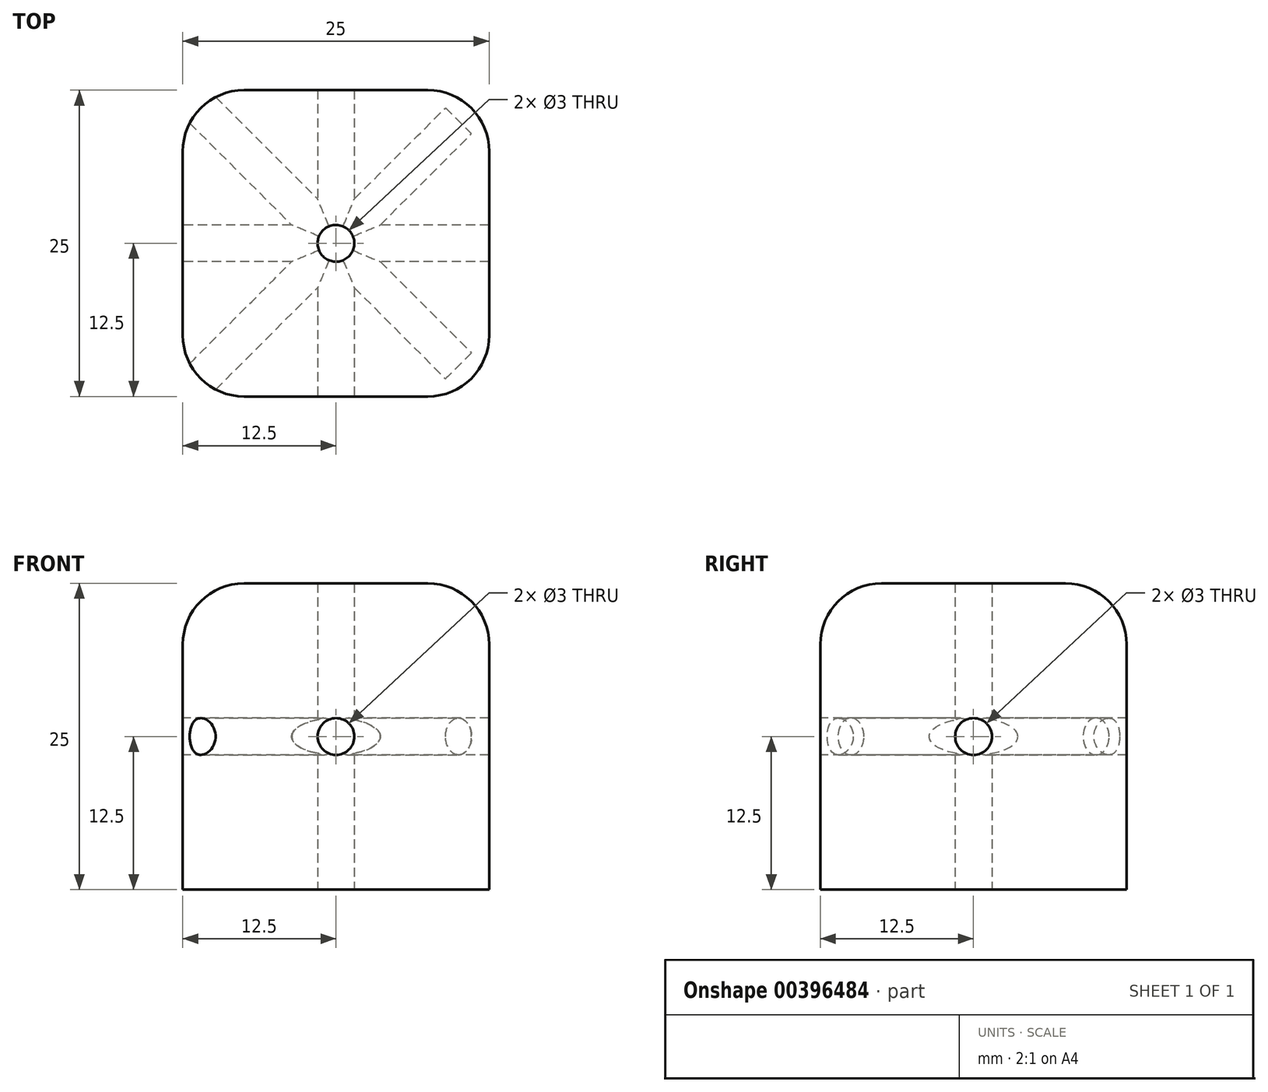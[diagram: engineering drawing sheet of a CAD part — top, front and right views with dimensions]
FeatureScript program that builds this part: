
annotation { "Feature Type Name" : "Feature", "Feature Type Description" : "" }
export const myFeature = defineFeature(function(context is Context, id is Id, definition is map)
    precondition{}
    {
        {
            var Q0;
            Q0=qCreatedBy(makeId("Front.planeOp"),FACE);
            var sketch = newSketch(context, id + "F0", { "sketchPlane" : qUnion([Q0])});
            skLineSegment(sketch, "E0.bottom", {"start": v(-12.5, -12.5) * mm, "end": v(12.5, -12.5) * mm});
            skLineSegment(sketch, "E0.top", {"start": v(-12.5, 12.5) * mm, "end": v(12.5, 12.5) * mm});
            skLineSegment(sketch, "E0.left", {"start": v(-12.5, -12.5) * mm, "end": v(-12.5, 12.5) * mm});
            skLineSegment(sketch, "E0.right", {"start": v(12.5, -12.5) * mm, "end": v(12.5, 12.5) * mm});
            skPoint(sketch, "E0.middle", {"position": v(0, 0) * mm});
            skSolve(sketch);
        }
        {
            var Q0;
            Q0=makeQuery(id+"F0.imprint","IMPRINT",FACE,{"disambiguationData":[TD([[makeQuery(id+"F0.imprint","IMPRINT",EDGE,{"derivedFrom":sQuery(id+"F0.wireOp",EDGE,"E0.bottom")}),1.0]])]});
            extrude(context, id + "F1", {"entities" : qUnion([Q0]), "endBound" : BoundingType.SYMMETRIC, "depth" : 25 * mm});
        }
        {
            var Q0;
            Q0=makeQuery(id+"F1.opExtrude","CAP_FACE",FACE,{"disambiguationData":[OSD([sQuery(id+"F0.wireOp",EDGE,"E0.bottom"),sQuery(id+"F0.wireOp",EDGE,"E0.top"),sQuery(id+"F0.wireOp",EDGE,"E0.left"),sQuery(id+"F0.wireOp",EDGE,"E0.right")])],"isStart":false});
            var sketch = newSketch(context, id + "F2", { "sketchPlane" : qUnion([Q0])});
            skCircle(sketch, "E1", {"center": v(0, 0) * mm, "radius": 1.5 * mm});
            skSolve(sketch);
        }
        {
            var Q0;
            Q0 = qSketchRegion(id + "F2", true);
            extrude(context, id + "F3", {"entities" : qUnion([Q0]), "operationType" : NewBodyOperationType.REMOVE, "endBound" : BoundingType.UP_TO_NEXT, "oppositeDirection" : true, "depth" : 25 * mm});
        }
        {
            var Q0;
            Q0=makeQuery(id+"F1.opExtrude","SWEPT_FACE",FACE,{"disambiguationData":[OSD([sQuery(id+"F0.wireOp",EDGE,"E0.bottom")])]});
            var sketch = newSketch(context, id + "F4", { "sketchPlane" : qUnion([Q0])});
            skCircle(sketch, "E2", {"center": v(0, 0) * mm, "radius": 1.5 * mm});
            skSolve(sketch);
        }
        {
            var Q0;
            Q0 = qSketchRegion(id + "F4", true);
            extrude(context, id + "F5", {"entities" : qUnion([Q0]), "operationType" : NewBodyOperationType.REMOVE, "endBound" : BoundingType.THROUGH_ALL, "oppositeDirection" : true, "depth" : 25 * mm});
        }
        {
            var Q0;
            Q0=makeQuery(id+"F1.opExtrude","SWEPT_FACE",FACE,{"disambiguationData":[OSD([sQuery(id+"F0.wireOp",EDGE,"E0.left")])]});
            var sketch = newSketch(context, id + "F6", { "sketchPlane" : qUnion([Q0])});
            skCircle(sketch, "E3", {"center": v(0, 0) * mm, "radius": 1.5 * mm});
            skSolve(sketch);
        }
        {
            var Q0;
            Q0=makeQuery(id+"F6.imprint","IMPRINT",FACE,{"disambiguationData":[TD([[makeQuery(id+"F6.imprint","IMPRINT",EDGE,{"derivedFrom":sQuery(id+"F6.wireOp",EDGE,"E3")}),1.0]])]});
            extrude(context, id + "F7", {"entities" : qUnion([Q0]), "operationType" : NewBodyOperationType.REMOVE, "endBound" : BoundingType.THROUGH_ALL, "oppositeDirection" : true, "depth" : 25 * mm});
        }
        {
            var Q0;
            Q0=makeQuery(id+"F1.opExtrude","CAP_EDGE",EDGE,{"disambiguationData":[OSD([sQuery(id+"F0.wireOp",EDGE,"E0.right")])],"isStart":false});
            var Q1;
            Q1=makeQuery(id+"F1.opExtrude","SWEPT_EDGE",EDGE,{"disambiguationData":[OSD([sQuery(id+"F0.wireOp",EDGE,"E0.top"),sQuery(id+"F0.wireOp",EDGE,"E0.right")])]});
            var Q2;
            Q2=makeQuery(id+"F1.opExtrude","CAP_EDGE",EDGE,{"disambiguationData":[OSD([sQuery(id+"F0.wireOp",EDGE,"E0.top")])],"isStart":true});
            var Q3;
            Q3=makeQuery(id+"F1.opExtrude","CAP_EDGE",EDGE,{"disambiguationData":[OSD([sQuery(id+"F0.wireOp",EDGE,"E0.left")])],"isStart":true});
            var Q4;
            Q4=makeQuery(id+"F1.opExtrude","SWEPT_EDGE",EDGE,{"disambiguationData":[OSD([sQuery(id+"F0.wireOp",EDGE,"E0.top"),sQuery(id+"F0.wireOp",EDGE,"E0.left")])]});
            var Q5;
            Q5=makeQuery(id+"F1.opExtrude","CAP_EDGE",EDGE,{"disambiguationData":[OSD([sQuery(id+"F0.wireOp",EDGE,"E0.left")])],"isStart":false});
            var Q6;
            Q6=makeQuery(id+"F1.opExtrude","CAP_EDGE",EDGE,{"disambiguationData":[OSD([sQuery(id+"F0.wireOp",EDGE,"E0.top")])],"isStart":false});
            var Q7;
            Q7=makeQuery(id+"F1.opExtrude","CAP_EDGE",EDGE,{"disambiguationData":[OSD([sQuery(id+"F0.wireOp",EDGE,"E0.right")])],"isStart":true});
            fillet(context, id + "F8", {"entities" : qUnion([Q0, Q1, Q2, Q3, Q4, Q5, Q6, Q7]), "radius" : 5 * mm, "tangentPropagation" : true, "allowEdgeOverflow" : false});
        }
        {
            var Q0;
            {var subQ0=sQuery(id+"F0.wireOp",EDGE,"E0.right");var subQ1=sQuery(id+"F0.wireOp",EDGE,"E0.top");Q0=makeQuery(id+"F8.opFillet","BLEND_VERTEX",VERTEX,{"blendedFrom":[makeQuery(id+"F1.opExtrude","CAP_VERTEX",VERTEX,{"disambiguationData":[OSD([subQ1,subQ0])],"isStart":true}),makeQuery(id+"F1.opExtrude","SWEPT_EDGE",EDGE,{"disambiguationData":[OSD([subQ1,subQ0])]}),makeQuery(id+"F1.opExtrude","CAP_EDGE",EDGE,{"disambiguationData":[OSD([subQ0])],"isStart":true}),makeQuery(id+"F1.opExtrude","SWEPT_FACE",FACE,{"disambiguationData":[OSD([subQ0])]})],"blendedInto":[makeQuery(id+"F1.opExtrude","SWEPT_FACE",FACE,{"disambiguationData":[OSD([subQ0])]})]});}
            var Q1;
            {var subQ0=sQuery(id+"F0.wireOp",EDGE,"E0.right");var subQ1=sQuery(id+"F0.wireOp",EDGE,"E0.top");Q1=makeQuery(id+"F8.opFillet","BLEND_VERTEX",VERTEX,{"blendedFrom":[makeQuery(id+"F1.opExtrude","CAP_VERTEX",VERTEX,{"disambiguationData":[OSD([subQ1,subQ0])],"isStart":true}),makeQuery(id+"F1.opExtrude","CAP_EDGE",EDGE,{"disambiguationData":[OSD([subQ1])],"isStart":true}),makeQuery(id+"F1.opExtrude","CAP_EDGE",EDGE,{"disambiguationData":[OSD([subQ0])],"isStart":true}),makeQuery(id+"F1.opExtrude","CAP_FACE",FACE,{"disambiguationData":[OSD([sQuery(id+"F0.wireOp",EDGE,"E0.bottom"),subQ1,sQuery(id+"F0.wireOp",EDGE,"E0.left"),subQ0])],"isStart":true})],"blendedInto":[makeQuery(id+"F1.opExtrude","CAP_FACE",FACE,{"disambiguationData":[OSD([sQuery(id+"F0.wireOp",EDGE,"E0.bottom"),subQ1,sQuery(id+"F0.wireOp",EDGE,"E0.left"),subQ0])],"isStart":true})]});}
            var Q2;
            {var subQ0=sQuery(id+"F0.wireOp",EDGE,"E0.right");Q2=makeQuery(id+"F8.opFillet","BLEND_VERTEX",VERTEX,{"blendedFrom":[makeQuery(id+"F1.opExtrude","CAP_EDGE",EDGE,{"disambiguationData":[OSD([subQ0])],"isStart":true}),makeQuery(id+"F1.opExtrude","SWEPT_FACE",FACE,{"disambiguationData":[OSD([sQuery(id+"F0.wireOp",EDGE,"E0.bottom")])]}),makeQuery(id+"F1.opExtrude","SWEPT_FACE",FACE,{"disambiguationData":[OSD([subQ0])]})],"blendedInto":[makeQuery(id+"F1.opExtrude","SWEPT_FACE",FACE,{"disambiguationData":[OSD([sQuery(id+"F0.wireOp",EDGE,"E0.bottom")])]}),makeQuery(id+"F1.opExtrude","SWEPT_FACE",FACE,{"disambiguationData":[OSD([subQ0])]})]});}
            cPlane(context, id + "F9", {"entities" : qUnion([Q0, Q1, Q2]), "cplaneType" : CPlaneType.THREE_POINT, "offset" : 25 * mm, "width" : 150 * mm, "height" : 150 * mm});
        }
        {
            var Q0;
            Q0=qCreatedBy(id+"F9.planeOp",FACE);
            var sketch = newSketch(context, id + "F10", { "sketchPlane" : qUnion([Q0])});
            skCircle(sketch, "E4", {"center": v(0, 0) * mm, "radius": 1.5 * mm});
            skSolve(sketch);
        }
        {
            var Q0;
            Q0 = qSketchRegion(id + "F10", true);
            extrude(context, id + "F11", {"entities" : qUnion([Q0]), "operationType" : NewBodyOperationType.REMOVE, "endBound" : BoundingType.THROUGH_ALL, "oppositeDirection" : true, "depth" : 25 * mm});
        }
        {
            var Q0;
            {var subQ0=sQuery(id+"F0.wireOp",EDGE,"E0.right");var subQ1=sQuery(id+"F0.wireOp",EDGE,"E0.top");Q0=makeQuery(id+"F8.opFillet","BLEND_VERTEX",VERTEX,{"blendedFrom":[makeQuery(id+"F1.opExtrude","CAP_VERTEX",VERTEX,{"disambiguationData":[OSD([subQ1,subQ0])],"isStart":false}),makeQuery(id+"F1.opExtrude","CAP_EDGE",EDGE,{"disambiguationData":[OSD([subQ1])],"isStart":false}),makeQuery(id+"F1.opExtrude","CAP_EDGE",EDGE,{"disambiguationData":[OSD([subQ0])],"isStart":false}),makeQuery(id+"F1.opExtrude","CAP_FACE",FACE,{"disambiguationData":[OSD([sQuery(id+"F0.wireOp",EDGE,"E0.bottom"),subQ1,sQuery(id+"F0.wireOp",EDGE,"E0.left"),subQ0])],"isStart":false})],"blendedInto":[makeQuery(id+"F1.opExtrude","CAP_FACE",FACE,{"disambiguationData":[OSD([sQuery(id+"F0.wireOp",EDGE,"E0.bottom"),subQ1,sQuery(id+"F0.wireOp",EDGE,"E0.left"),subQ0])],"isStart":false})]});}
            var Q1;
            {var subQ0=sQuery(id+"F0.wireOp",EDGE,"E0.right");var subQ1=sQuery(id+"F0.wireOp",EDGE,"E0.top");Q1=makeQuery(id+"F8.opFillet","BLEND_VERTEX",VERTEX,{"blendedFrom":[makeQuery(id+"F1.opExtrude","CAP_VERTEX",VERTEX,{"disambiguationData":[OSD([subQ1,subQ0])],"isStart":false}),makeQuery(id+"F1.opExtrude","SWEPT_EDGE",EDGE,{"disambiguationData":[OSD([subQ1,subQ0])]}),makeQuery(id+"F1.opExtrude","CAP_EDGE",EDGE,{"disambiguationData":[OSD([subQ0])],"isStart":false}),makeQuery(id+"F1.opExtrude","SWEPT_FACE",FACE,{"disambiguationData":[OSD([subQ0])]})],"blendedInto":[makeQuery(id+"F1.opExtrude","SWEPT_FACE",FACE,{"disambiguationData":[OSD([subQ0])]})]});}
            var Q2;
            {var subQ0=sQuery(id+"F0.wireOp",EDGE,"E0.bottom");var subQ1=sQuery(id+"F0.wireOp",EDGE,"E0.right");Q2=makeQuery(id+"F8.opFillet","BLEND_VERTEX",VERTEX,{"blendedFrom":[makeQuery(id+"F1.opExtrude","CAP_EDGE",EDGE,{"disambiguationData":[OSD([subQ1])],"isStart":false}),makeQuery(id+"F1.opExtrude","CAP_FACE",FACE,{"disambiguationData":[OSD([subQ0,sQuery(id+"F0.wireOp",EDGE,"E0.top"),sQuery(id+"F0.wireOp",EDGE,"E0.left"),subQ1])],"isStart":false}),makeQuery(id+"F1.opExtrude","SWEPT_FACE",FACE,{"disambiguationData":[OSD([subQ0])]})],"blendedInto":[makeQuery(id+"F1.opExtrude","CAP_FACE",FACE,{"disambiguationData":[OSD([subQ0,sQuery(id+"F0.wireOp",EDGE,"E0.top"),sQuery(id+"F0.wireOp",EDGE,"E0.left"),subQ1])],"isStart":false}),makeQuery(id+"F1.opExtrude","SWEPT_FACE",FACE,{"disambiguationData":[OSD([subQ0])]})]});}
            cPlane(context, id + "F12", {"entities" : qUnion([Q0, Q1, Q2]), "cplaneType" : CPlaneType.THREE_POINT, "offset" : 25 * mm, "width" : 150 * mm, "height" : 150 * mm});
        }
        {
            var Q0;
            Q0=qCreatedBy(id+"F12.planeOp",FACE);
            var sketch = newSketch(context, id + "F13", { "sketchPlane" : qUnion([Q0])});
            skCircle(sketch, "E5", {"center": v(0, 0) * mm, "radius": 1.5 * mm});
            skSolve(sketch);
        }
        {
            var Q0;
            Q0 = qSketchRegion(id + "F13", true);
            extrude(context, id + "F14", {"entities" : qUnion([Q0]), "operationType" : NewBodyOperationType.REMOVE, "endBound" : BoundingType.THROUGH_ALL, "oppositeDirection" : true, "depth" : 25 * mm});
        }
    });
